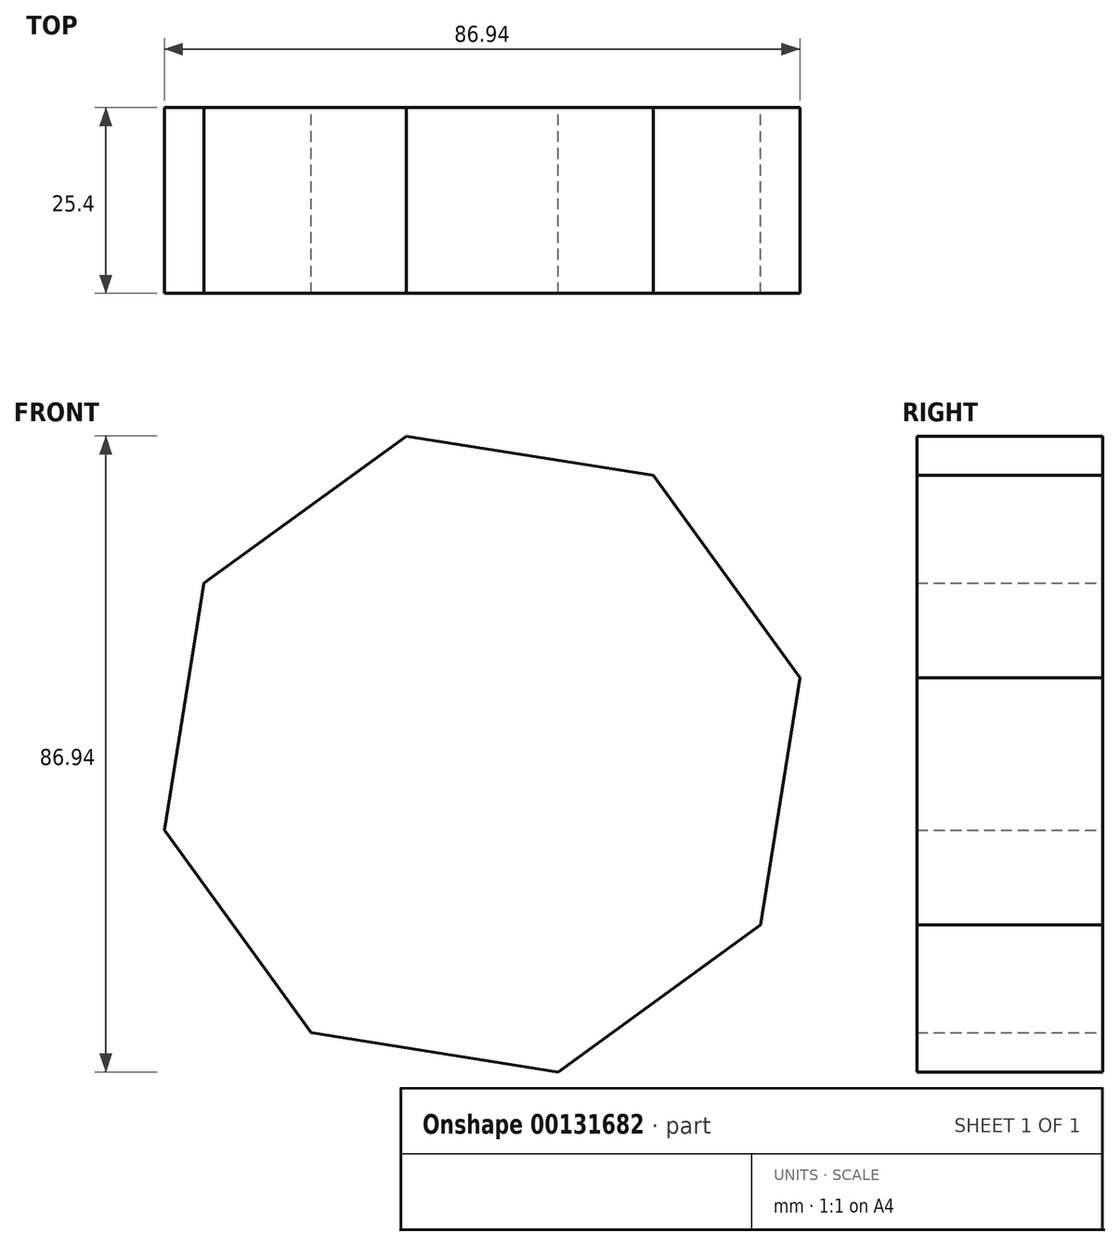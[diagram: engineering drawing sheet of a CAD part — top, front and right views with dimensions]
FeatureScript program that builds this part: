
annotation { "Feature Type Name" : "Feature", "Feature Type Description" : "" }
export const myFeature = defineFeature(function(context is Context, id is Id, definition is map)
    precondition{}
    {
        {
            var Q0;
            Q0=qCreatedBy(makeId("Front.planeOp"),FACE);
            var sketch = newSketch(context, id + "F0", { "sketchPlane" : qUnion([Q0])});
            skCircle(sketch, "E0.cCircle", {"center": v(0, 0) * mm, "radius": 44.69 * mm, "construction": true});
            skLineSegment(sketch, "E0.0", {"start": v(23.39, 38.08) * mm, "end": v(43.47, 10.39) * mm});
            skLineSegment(sketch, "E0.1", {"start": v(43.47, 10.39) * mm, "end": v(38.08, -23.39) * mm});
            skLineSegment(sketch, "E0.2", {"start": v(38.08, -23.39) * mm, "end": v(10.39, -43.47) * mm});
            skLineSegment(sketch, "E0.3", {"start": v(10.39, -43.47) * mm, "end": v(-23.39, -38.08) * mm});
            skLineSegment(sketch, "E0.4", {"start": v(-23.39, -38.08) * mm, "end": v(-43.47, -10.39) * mm});
            skLineSegment(sketch, "E0.5", {"start": v(-43.47, -10.39) * mm, "end": v(-38.08, 23.39) * mm});
            skLineSegment(sketch, "E0.6", {"start": v(-38.08, 23.39) * mm, "end": v(-10.39, 43.47) * mm});
            skLineSegment(sketch, "E0.7", {"start": v(-10.39, 43.47) * mm, "end": v(23.39, 38.08) * mm});
            skSolve(sketch);
        }
        {
            var Q0;
            Q0=makeQuery(id+"F0.imprint","IMPRINT",FACE,{"disambiguationData":[TD([[makeQuery(id+"F0.imprint","IMPRINT",EDGE,{"derivedFrom":sQuery(id+"F0.wireOp",EDGE,"E0.0")}),-1.0]])]});
            extrude(context, id + "F1", {"entities" : qUnion([Q0]), "endBound" : BoundingType.SYMMETRIC, "depth" : 25.4 * mm});
        }
    });
